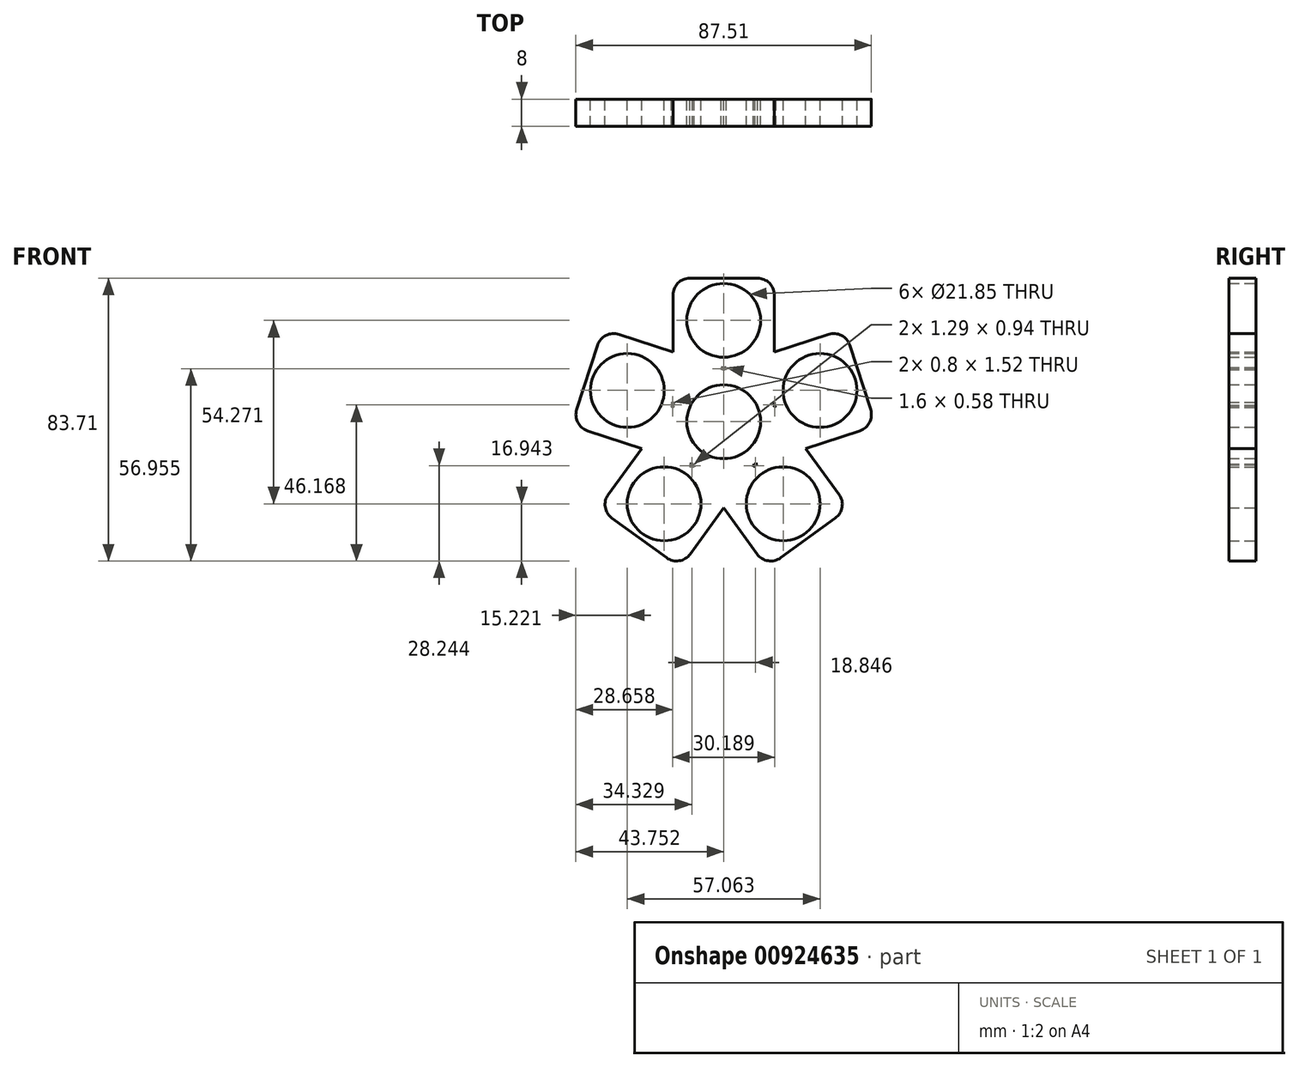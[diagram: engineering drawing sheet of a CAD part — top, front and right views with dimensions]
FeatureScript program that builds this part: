
annotation { "Feature Type Name" : "Feature", "Feature Type Description" : "" }
export const myFeature = defineFeature(function(context is Context, id is Id, definition is map)
    precondition{}
    {
        {
            var Q0;
            Q0=qCreatedBy(makeId("Front.planeOp"),FACE);
            var sketch = newSketch(context, id + "F0", { "sketchPlane" : qUnion([Q0])});
            skCircle(sketch, "E0", {"center": v(147.66, 55.6) * mm, "radius": 10.93 * mm});
            skLineSegment(sketch, "E1", {"start": v(147.66, 85.6) * mm, "end": v(147.66, 55.6) * mm, "construction": true});
            skCircle(sketch, "E2", {"center": v(147.66, 85.6) * mm, "radius": 10.93 * mm});
            skPoint(sketch, "E3", {"position": v(147.66, 70.6) * mm});
            skLineSegment(sketch, "E4.bottom", {"start": v(162.66, 43.1) * mm, "end": v(132.66, 43.1) * mm});
            skLineSegment(sketch, "E4.top", {"start": v(157.66, 98.1) * mm, "end": v(137.66, 98.1) * mm});
            skLineSegment(sketch, "E4.left", {"start": v(162.66, 43.1) * mm, "end": v(162.66, 93.1) * mm});
            skLineSegment(sketch, "E4.right", {"start": v(132.66, 43.1) * mm, "end": v(132.66, 93.1) * mm});
            skPoint(sketch, "E5.visualSharp", {"position": v(132.66, 98.1) * mm});
            skArc(sketch, "E5.filletArc", {"start": v(137.66, 98.1) * mm, "mid": v(134.13, 96.63) * mm, "end": v(132.66, 93.1) * mm});
            skPoint(sketch, "E6.visualSharp", {"position": v(162.66, 98.1) * mm});
            skArc(sketch, "E6.filletArc", {"start": v(162.66, 93.1) * mm, "mid": v(161.2, 96.63) * mm, "end": v(157.66, 98.1) * mm});
            skPoint(sketch, "E7.1.0", {"position": v(102.6, 54.46) * mm});
            skLineSegment(sketch, "E7.1.1", {"start": v(119.13, 64.86) * mm, "end": v(147.66, 55.6) * mm, "construction": true});
            skLineSegment(sketch, "E7.1.2", {"start": v(110.33, 78.24) * mm, "end": v(104.15, 59.22) * mm});
            skLineSegment(sketch, "E7.1.3", {"start": v(154.92, 37.47) * mm, "end": v(107.36, 52.92) * mm});
            skPoint(sketch, "E7.1.4", {"position": v(111.88, 83) * mm});
            skArc(sketch, "E7.1.5", {"start": v(116.63, 81.45) * mm, "mid": v(112.82, 81.15) * mm, "end": v(110.33, 78.24) * mm});
            skLineSegment(sketch, "E7.1.7", {"start": v(164.19, 66) * mm, "end": v(116.63, 81.45) * mm});
            skLineSegment(sketch, "E7.1.8", {"start": v(164.19, 66) * mm, "end": v(154.92, 37.47) * mm});
            skCircle(sketch, "E7.1.9", {"center": v(119.13, 64.86) * mm, "radius": 10.92 * mm});
            skPoint(sketch, "E7.1.10", {"position": v(133.4, 60.23) * mm});
            skPoint(sketch, "E7.1.11", {"position": v(133.4, 60.23) * mm});
            skArc(sketch, "E7.1.12", {"start": v(104.15, 59.22) * mm, "mid": v(104.45, 55.4) * mm, "end": v(107.36, 52.92) * mm});
            skPoint(sketch, "E7.2.0", {"position": v(134.82, 12.4) * mm});
            skLineSegment(sketch, "E7.2.1", {"start": v(130.03, 31.32) * mm, "end": v(147.66, 55.6) * mm, "construction": true});
            skLineSegment(sketch, "E7.2.2", {"start": v(114.6, 27.09) * mm, "end": v(130.77, 15.33) * mm});
            skLineSegment(sketch, "E7.2.3", {"start": v(167.15, 56.89) * mm, "end": v(137.76, 16.44) * mm});
            skPoint(sketch, "E7.2.4", {"position": v(110.55, 30.03) * mm});
            skArc(sketch, "E7.2.5", {"start": v(113.49, 34.07) * mm, "mid": v(112.6, 30.35) * mm, "end": v(114.6, 27.09) * mm});
            skLineSegment(sketch, "E7.2.7", {"start": v(142.87, 74.52) * mm, "end": v(113.49, 34.07) * mm});
            skLineSegment(sketch, "E7.2.8", {"start": v(142.87, 74.52) * mm, "end": v(167.15, 56.89) * mm});
            skCircle(sketch, "E7.2.9", {"center": v(130.03, 31.32) * mm, "radius": 10.93 * mm});
            skPoint(sketch, "E7.2.10", {"position": v(138.85, 43.46) * mm});
            skPoint(sketch, "E7.2.11", {"position": v(138.85, 43.46) * mm});
            skArc(sketch, "E7.2.12", {"start": v(130.77, 15.33) * mm, "mid": v(134.5, 14.44) * mm, "end": v(137.76, 16.44) * mm});
            skLineSegment(sketch, "E8.1.3.0", {"start": v(165.3, 31.32) * mm, "end": v(147.66, 55.6) * mm, "construction": true});
            skLineSegment(sketch, "E8.4.3.0", {"start": v(164.55, 15.33) * mm, "end": v(180.73, 27.09) * mm});
            skLineSegment(sketch, "E8.7.3.0", {"start": v(152.45, 74.52) * mm, "end": v(181.84, 34.07) * mm});
            skPoint(sketch, "E8.8.3.0", {"position": v(184.78, 30.03) * mm});
            skPoint(sketch, "E8.10.3.0", {"position": v(160.5, 12.4) * mm});
            skArc(sketch, "E8.11.3.0", {"start": v(157.57, 16.44) * mm, "mid": v(160.83, 14.44) * mm, "end": v(164.55, 15.33) * mm});
            skLineSegment(sketch, "E8.17.3.0", {"start": v(128.18, 56.89) * mm, "end": v(157.57, 16.44) * mm});
            skLineSegment(sketch, "E8.20.3.0", {"start": v(128.18, 56.89) * mm, "end": v(152.45, 74.52) * mm});
            skCircle(sketch, "E8.23.3.0", {"center": v(165.3, 31.32) * mm, "radius": 10.93 * mm});
            skPoint(sketch, "E8.25.3.0", {"position": v(156.48, 43.46) * mm});
            skPoint(sketch, "E8.26.3.0", {"position": v(156.48, 43.46) * mm});
            skArc(sketch, "E8.27.3.0", {"start": v(180.73, 27.09) * mm, "mid": v(182.73, 30.35) * mm, "end": v(181.84, 34.07) * mm});
            skLineSegment(sketch, "E8.1.4.0", {"start": v(176.2, 64.86) * mm, "end": v(147.66, 55.6) * mm, "construction": true});
            skLineSegment(sketch, "E8.4.4.0", {"start": v(191.17, 59.22) * mm, "end": v(185, 78.24) * mm});
            skLineSegment(sketch, "E8.7.4.0", {"start": v(131.14, 66) * mm, "end": v(178.7, 81.45) * mm});
            skPoint(sketch, "E8.8.4.0", {"position": v(183.45, 83) * mm});
            skPoint(sketch, "E8.10.4.0", {"position": v(192.72, 54.46) * mm});
            skArc(sketch, "E8.11.4.0", {"start": v(187.96, 52.92) * mm, "mid": v(190.87, 55.4) * mm, "end": v(191.17, 59.22) * mm});
            skLineSegment(sketch, "E8.17.4.0", {"start": v(140.4, 37.47) * mm, "end": v(187.96, 52.92) * mm});
            skLineSegment(sketch, "E8.20.4.0", {"start": v(140.4, 37.47) * mm, "end": v(131.14, 66) * mm});
            skCircle(sketch, "E8.23.4.0", {"center": v(176.2, 64.86) * mm, "radius": 10.93 * mm});
            skPoint(sketch, "E8.25.4.0", {"position": v(161.93, 60.23) * mm});
            skPoint(sketch, "E8.26.4.0", {"position": v(161.93, 60.23) * mm});
            skArc(sketch, "E8.27.4.0", {"start": v(185, 78.24) * mm, "mid": v(182.5, 81.15) * mm, "end": v(178.7, 81.45) * mm});
            skSolve(sketch);
        }
        {
            var Q0;
            {var subQ0=sQuery(id+"F0.wireOp",EDGE,"E8.17.3.0");var subQ1=sQuery(id+"F0.wireOp",EDGE,"E4.bottom");var subQ2=makeQuery(id+"F0.imprint","INTERSECT",VERTEX,{"derivedFrom":[subQ1,subQ0]});Q0=makeQuery(id+"F0.imprint","IMPRINT",FACE,{"disambiguationData":[TD([[makeQuery(id+"F0.imprint","IMPRINT",EDGE,{"disambiguationData":[TD([[subQ2,-1.0]])],"derivedFrom":subQ1}),-1.0]])]});}
            var Q1;
            {var subQ0=sQuery(id+"F0.wireOp",EDGE,"E7.1.7");var subQ1=sQuery(id+"F0.wireOp",EDGE,"E4.right");var subQ2=makeQuery(id+"F0.imprint","INTERSECT",VERTEX,{"derivedFrom":[subQ1,subQ0]});Q1=makeQuery(id+"F0.imprint","IMPRINT",FACE,{"disambiguationData":[TD([[makeQuery(id+"F0.imprint","IMPRINT",EDGE,{"disambiguationData":[TD([[subQ2,1.0]])],"derivedFrom":subQ1}),-1.0]])]});}
            var Q2;
            Q2=makeQuery(id+"F0.imprint","IMPRINT",FACE,{"disambiguationData":[TD([[makeQuery(id+"F0.imprint","IMPRINT",EDGE,{"derivedFrom":sQuery(id+"F0.wireOp",EDGE,"E2")}),-1.0]])]});
            var Q3;
            {var subQ0=sQuery(id+"F0.wireOp",EDGE,"E8.7.4.0");var subQ1=sQuery(id+"F0.wireOp",EDGE,"E4.left");var subQ2=makeQuery(id+"F0.imprint","INTERSECT",VERTEX,{"derivedFrom":[subQ1,subQ0]});Q3=makeQuery(id+"F0.imprint","IMPRINT",FACE,{"disambiguationData":[TD([[makeQuery(id+"F0.imprint","IMPRINT",EDGE,{"disambiguationData":[TD([[subQ2,1.0]])],"derivedFrom":subQ1}),1.0]])]});}
            var Q4;
            {var subQ0=sQuery(id+"F0.wireOp",EDGE,"E8.7.3.0");var subQ1=sQuery(id+"F0.wireOp",EDGE,"E7.1.7");var subQ2=makeQuery(id+"F0.imprint","INTERSECT",VERTEX,{"derivedFrom":[subQ1,subQ0]});Q4=makeQuery(id+"F0.imprint","IMPRINT",FACE,{"disambiguationData":[TD([[makeQuery(id+"F0.imprint","IMPRINT",EDGE,{"disambiguationData":[TD([[subQ2,-1.0]])],"derivedFrom":subQ1}),-1.0]])]});}
            var Q5;
            Q5=makeQuery(id+"F0.imprint","IMPRINT",FACE,{"disambiguationData":[TD([[makeQuery(id+"F0.imprint","IMPRINT",EDGE,{"derivedFrom":sQuery(id+"F0.wireOp",EDGE,"E0")}),-1.0]])]});
            var Q6;
            {var subQ0=sQuery(id+"F0.wireOp",EDGE,"E7.2.3");var subQ1=sQuery(id+"F0.wireOp",EDGE,"E7.1.3");var subQ2=makeQuery(id+"F0.imprint","INTERSECT",VERTEX,{"derivedFrom":[subQ1,subQ0]});Q6=makeQuery(id+"F0.imprint","IMPRINT",FACE,{"disambiguationData":[TD([[makeQuery(id+"F0.imprint","IMPRINT",EDGE,{"disambiguationData":[TD([[subQ2,-1.0]])],"derivedFrom":subQ1}),1.0]])]});}
            var Q7;
            Q7=makeQuery(id+"F0.imprint","IMPRINT",FACE,{"disambiguationData":[TD([[makeQuery(id+"F0.imprint","IMPRINT",EDGE,{"derivedFrom":sQuery(id+"F0.wireOp",EDGE,"E7.2.2")}),1.0]])]});
            var Q8;
            Q8=makeQuery(id+"F0.imprint","IMPRINT",FACE,{"disambiguationData":[TD([[makeQuery(id+"F0.imprint","IMPRINT",EDGE,{"derivedFrom":sQuery(id+"F0.wireOp",EDGE,"E8.4.3.0")}),1.0]])]});
            var Q9;
            Q9=makeQuery(id+"F0.imprint","IMPRINT",FACE,{"disambiguationData":[TD([[makeQuery(id+"F0.imprint","IMPRINT",EDGE,{"derivedFrom":sQuery(id+"F0.wireOp",EDGE,"E8.4.4.0")}),1.0]])]});
            var Q10;
            {var subQ0=sQuery(id+"F0.wireOp",EDGE,"E8.17.4.0");var subQ1=sQuery(id+"F0.wireOp",EDGE,"E4.left");var subQ2=makeQuery(id+"F0.imprint","INTERSECT",VERTEX,{"derivedFrom":[subQ1,subQ0]});Q10=makeQuery(id+"F0.imprint","IMPRINT",FACE,{"disambiguationData":[TD([[makeQuery(id+"F0.imprint","IMPRINT",EDGE,{"disambiguationData":[TD([[subQ2,-1.0]])],"derivedFrom":subQ1}),-1.0]])]});}
            var Q11;
            {var subQ0=sQuery(id+"F0.wireOp",EDGE,"E7.2.3");var subQ1=sQuery(id+"F0.wireOp",EDGE,"E4.left");var subQ2=makeQuery(id+"F0.imprint","INTERSECT",VERTEX,{"derivedFrom":[subQ1,subQ0]});Q11=makeQuery(id+"F0.imprint","IMPRINT",FACE,{"disambiguationData":[TD([[makeQuery(id+"F0.imprint","IMPRINT",EDGE,{"disambiguationData":[TD([[subQ2,-1.0]])],"derivedFrom":subQ1}),-1.0]])]});}
            var Q12;
            {var subQ0=sQuery(id+"F0.wireOp",EDGE,"E7.2.8");var subQ1=sQuery(id+"F0.wireOp",EDGE,"E7.2.3");var subQ2=makeQuery(id+"F0.imprint","INTERSECT",VERTEX,{"derivedFrom":[subQ1,subQ0]});Q12=makeQuery(id+"F0.imprint","IMPRINT",FACE,{"disambiguationData":[TD([[makeQuery(id+"F0.imprint","IMPRINT",EDGE,{"disambiguationData":[TD([[subQ2,-1.0]])],"derivedFrom":subQ1}),-1.0]])]});}
            var Q13;
            {var subQ0=sQuery(id+"F0.wireOp",EDGE,"E7.2.3");var subQ1=sQuery(id+"F0.wireOp",EDGE,"E4.bottom");var subQ2=makeQuery(id+"F0.imprint","INTERSECT",VERTEX,{"derivedFrom":[subQ1,subQ0]});Q13=makeQuery(id+"F0.imprint","IMPRINT",FACE,{"disambiguationData":[TD([[makeQuery(id+"F0.imprint","IMPRINT",EDGE,{"disambiguationData":[TD([[subQ2,-1.0]])],"derivedFrom":subQ1}),-1.0]])]});}
            var Q14;
            {var subQ0=sQuery(id+"F0.wireOp",EDGE,"E8.17.4.0");var subQ1=sQuery(id+"F0.wireOp",EDGE,"E4.bottom");var subQ2=makeQuery(id+"F0.imprint","INTERSECT",VERTEX,{"derivedFrom":[subQ1,subQ0]});Q14=makeQuery(id+"F0.imprint","IMPRINT",FACE,{"disambiguationData":[TD([[makeQuery(id+"F0.imprint","IMPRINT",EDGE,{"disambiguationData":[TD([[subQ2,-1.0]])],"derivedFrom":subQ1}),-1.0]])]});}
            var Q15;
            {var subQ0=sQuery(id+"F0.wireOp",EDGE,"E4.left");var subQ1=sQuery(id+"F0.wireOp",EDGE,"E4.bottom");var subQ2=makeQuery(id+"F0.imprint","INTERSECT",VERTEX,{"derivedFrom":[subQ1,subQ0]});Q15=makeQuery(id+"F0.imprint","IMPRINT",FACE,{"disambiguationData":[TD([[makeQuery(id+"F0.imprint","IMPRINT",EDGE,{"disambiguationData":[TD([[subQ2,-1.0]])],"derivedFrom":subQ1}),-1.0]])]});}
            var Q16;
            {var subQ0=sQuery(id+"F0.wireOp",EDGE,"E7.1.8");var subQ1=sQuery(id+"F0.wireOp",EDGE,"E7.1.3");var subQ2=makeQuery(id+"F0.imprint","INTERSECT",VERTEX,{"derivedFrom":[subQ1,subQ0]});Q16=makeQuery(id+"F0.imprint","IMPRINT",FACE,{"disambiguationData":[TD([[makeQuery(id+"F0.imprint","IMPRINT",EDGE,{"disambiguationData":[TD([[subQ2,-1.0]])],"derivedFrom":subQ1}),-1.0]])]});}
            var Q17;
            {var subQ0=sQuery(id+"F0.wireOp",EDGE,"E7.2.3");var subQ1=sQuery(id+"F0.wireOp",EDGE,"E7.1.3");var subQ2=makeQuery(id+"F0.imprint","INTERSECT",VERTEX,{"derivedFrom":[subQ1,subQ0]});Q17=makeQuery(id+"F0.imprint","IMPRINT",FACE,{"disambiguationData":[TD([[makeQuery(id+"F0.imprint","IMPRINT",EDGE,{"disambiguationData":[TD([[subQ2,-1.0]])],"derivedFrom":subQ1}),-1.0]])]});}
            var Q18;
            {var subQ3=sQuery(id+"F0.wireOp",EDGE,"E7.1.8");var subQ7=sQuery(id+"F0.wireOp",EDGE,"E4.bottom");var subQ9=makeQuery(id+"F0.imprint","INTERSECT",VERTEX,{"derivedFrom":[subQ7,subQ3]});Q18=makeQuery(id+"F0.imprint","IMPRINT",FACE,{"disambiguationData":[TD([[makeQuery(id+"F0.imprint","IMPRINT",EDGE,{"disambiguationData":[TD([[subQ9,-1.0]])],"derivedFrom":subQ7}),1.0]])]});}
            var Q19;
            {var subQ0=sQuery(id+"F0.wireOp",EDGE,"E8.17.4.0");var subQ1=sQuery(id+"F0.wireOp",EDGE,"E7.1.3");var subQ2=makeQuery(id+"F0.imprint","INTERSECT",VERTEX,{"derivedFrom":[subQ1,subQ0]});Q19=makeQuery(id+"F0.imprint","IMPRINT",FACE,{"disambiguationData":[TD([[makeQuery(id+"F0.imprint","IMPRINT",EDGE,{"disambiguationData":[TD([[subQ2,-1.0]])],"derivedFrom":subQ1}),1.0]])]});}
            var Q20;
            {var subQ0=sQuery(id+"F0.wireOp",EDGE,"E8.20.4.0");var subQ1=sQuery(id+"F0.wireOp",EDGE,"E8.17.3.0");var subQ2=makeQuery(id+"F0.imprint","INTERSECT",VERTEX,{"derivedFrom":[subQ1,subQ0]});Q20=makeQuery(id+"F0.imprint","IMPRINT",FACE,{"disambiguationData":[TD([[makeQuery(id+"F0.imprint","IMPRINT",EDGE,{"disambiguationData":[TD([[subQ2,-1.0]])],"derivedFrom":subQ1}),-1.0]])]});}
            var Q21;
            {var subQ3=sQuery(id+"F0.wireOp",EDGE,"E8.20.4.0");var subQ6=sQuery(id+"F0.wireOp",EDGE,"E4.bottom");var subQ9=makeQuery(id+"F0.imprint","INTERSECT",VERTEX,{"derivedFrom":[subQ6,subQ3]});Q21=makeQuery(id+"F0.imprint","IMPRINT",FACE,{"disambiguationData":[TD([[makeQuery(id+"F0.imprint","IMPRINT",EDGE,{"disambiguationData":[TD([[subQ9,-1.0]])],"derivedFrom":subQ6}),-1.0]])]});}
            var Q22;
            {var subQ0=sQuery(id+"F0.wireOp",EDGE,"E4.right");var subQ1=sQuery(id+"F0.wireOp",EDGE,"E4.bottom");var subQ2=makeQuery(id+"F0.imprint","INTERSECT",VERTEX,{"derivedFrom":[subQ1,subQ0]});Q22=makeQuery(id+"F0.imprint","IMPRINT",FACE,{"disambiguationData":[TD([[makeQuery(id+"F0.imprint","IMPRINT",EDGE,{"disambiguationData":[TD([[subQ2,1.0]])],"derivedFrom":subQ1}),-1.0]])]});}
            var Q23;
            {var subQ0=sQuery(id+"F0.wireOp",EDGE,"E7.1.3");var subQ1=sQuery(id+"F0.wireOp",EDGE,"E4.right");var subQ2=makeQuery(id+"F0.imprint","INTERSECT",VERTEX,{"derivedFrom":[subQ1,subQ0]});Q23=makeQuery(id+"F0.imprint","IMPRINT",FACE,{"disambiguationData":[TD([[makeQuery(id+"F0.imprint","IMPRINT",EDGE,{"disambiguationData":[TD([[subQ2,-1.0]])],"derivedFrom":subQ1}),1.0]])]});}
            var Q24;
            {var subQ0=sQuery(id+"F0.wireOp",EDGE,"E8.17.3.0");var subQ1=sQuery(id+"F0.wireOp",EDGE,"E4.right");var subQ2=makeQuery(id+"F0.imprint","INTERSECT",VERTEX,{"derivedFrom":[subQ1,subQ0]});Q24=makeQuery(id+"F0.imprint","IMPRINT",FACE,{"disambiguationData":[TD([[makeQuery(id+"F0.imprint","IMPRINT",EDGE,{"disambiguationData":[TD([[subQ2,-1.0]])],"derivedFrom":subQ1}),1.0]])]});}
            var Q25;
            {var subQ0=sQuery(id+"F0.wireOp",EDGE,"E8.20.3.0");var subQ1=sQuery(id+"F0.wireOp",EDGE,"E7.2.7");var subQ2=makeQuery(id+"F0.imprint","INTERSECT",VERTEX,{"derivedFrom":[subQ1,subQ0]});Q25=makeQuery(id+"F0.imprint","IMPRINT",FACE,{"disambiguationData":[TD([[makeQuery(id+"F0.imprint","IMPRINT",EDGE,{"disambiguationData":[TD([[subQ2,-1.0]])],"derivedFrom":subQ1}),-1.0]])]});}
            var Q26;
            {var subQ0=sQuery(id+"F0.wireOp",EDGE,"E8.20.4.0");var subQ1=sQuery(id+"F0.wireOp",EDGE,"E4.right");var subQ2=makeQuery(id+"F0.imprint","INTERSECT",VERTEX,{"derivedFrom":[subQ1,subQ0]});Q26=makeQuery(id+"F0.imprint","IMPRINT",FACE,{"disambiguationData":[TD([[makeQuery(id+"F0.imprint","IMPRINT",EDGE,{"disambiguationData":[TD([[subQ2,-1.0]])],"derivedFrom":subQ1}),-1.0]])]});}
            var Q27;
            {var subQ0=sQuery(id+"F0.wireOp",EDGE,"E8.20.4.0");var subQ1=sQuery(id+"F0.wireOp",EDGE,"E4.right");var subQ2=makeQuery(id+"F0.imprint","INTERSECT",VERTEX,{"derivedFrom":[subQ1,subQ0]});Q27=makeQuery(id+"F0.imprint","IMPRINT",FACE,{"disambiguationData":[TD([[makeQuery(id+"F0.imprint","IMPRINT",EDGE,{"disambiguationData":[TD([[subQ2,-1.0]])],"derivedFrom":subQ1}),1.0]])]});}
            var Q28;
            {var subQ5=sQuery(id+"F0.wireOp",EDGE,"E8.7.4.0");var subQ7=sQuery(id+"F0.wireOp",EDGE,"E7.2.7");var subQ8=makeQuery(id+"F0.imprint","INTERSECT",VERTEX,{"derivedFrom":[subQ7,subQ5]});Q28=makeQuery(id+"F0.imprint","IMPRINT",FACE,{"disambiguationData":[TD([[makeQuery(id+"F0.imprint","IMPRINT",EDGE,{"disambiguationData":[TD([[subQ8,-1.0]])],"derivedFrom":subQ7}),1.0]])]});}
            var Q29;
            {var subQ0=sQuery(id+"F0.wireOp",EDGE,"E7.2.8");var subQ1=sQuery(id+"F0.wireOp",EDGE,"E7.1.7");var subQ2=makeQuery(id+"F0.imprint","INTERSECT",VERTEX,{"derivedFrom":[subQ1,subQ0]});Q29=makeQuery(id+"F0.imprint","IMPRINT",FACE,{"disambiguationData":[TD([[makeQuery(id+"F0.imprint","IMPRINT",EDGE,{"disambiguationData":[TD([[subQ2,-1.0]])],"derivedFrom":subQ1}),-1.0]])]});}
            var Q30;
            {var subQ0=sQuery(id+"F0.wireOp",EDGE,"E7.2.8");var subQ1=sQuery(id+"F0.wireOp",EDGE,"E7.1.7");var subQ2=makeQuery(id+"F0.imprint","INTERSECT",VERTEX,{"derivedFrom":[subQ1,subQ0]});Q30=makeQuery(id+"F0.imprint","IMPRINT",FACE,{"disambiguationData":[TD([[makeQuery(id+"F0.imprint","IMPRINT",EDGE,{"disambiguationData":[TD([[subQ2,-1.0]])],"derivedFrom":subQ1}),1.0]])]});}
            var Q31;
            {var subQ5=sQuery(id+"F0.wireOp",EDGE,"E8.7.3.0");var subQ7=sQuery(id+"F0.wireOp",EDGE,"E7.1.7");var subQ8=makeQuery(id+"F0.imprint","INTERSECT",VERTEX,{"derivedFrom":[subQ7,subQ5]});Q31=makeQuery(id+"F0.imprint","IMPRINT",FACE,{"disambiguationData":[TD([[makeQuery(id+"F0.imprint","IMPRINT",EDGE,{"disambiguationData":[TD([[subQ8,-1.0]])],"derivedFrom":subQ7}),1.0]])]});}
            var Q32;
            {var subQ0=sQuery(id+"F0.wireOp",EDGE,"E7.1.8");var subQ1=sQuery(id+"F0.wireOp",EDGE,"E4.left");var subQ2=makeQuery(id+"F0.imprint","INTERSECT",VERTEX,{"derivedFrom":[subQ1,subQ0]});Q32=makeQuery(id+"F0.imprint","IMPRINT",FACE,{"disambiguationData":[TD([[makeQuery(id+"F0.imprint","IMPRINT",EDGE,{"disambiguationData":[TD([[subQ2,-1.0]])],"derivedFrom":subQ1}),1.0]])]});}
            var Q33;
            {var subQ0=sQuery(id+"F0.wireOp",EDGE,"E7.1.8");var subQ1=sQuery(id+"F0.wireOp",EDGE,"E4.left");var subQ2=makeQuery(id+"F0.imprint","INTERSECT",VERTEX,{"derivedFrom":[subQ1,subQ0]});Q33=makeQuery(id+"F0.imprint","IMPRINT",FACE,{"disambiguationData":[TD([[makeQuery(id+"F0.imprint","IMPRINT",EDGE,{"disambiguationData":[TD([[subQ2,-1.0]])],"derivedFrom":subQ1}),-1.0]])]});}
            var Q34;
            {var subQ0=sQuery(id+"F0.wireOp",EDGE,"E8.20.3.0");var subQ1=sQuery(id+"F0.wireOp",EDGE,"E8.7.3.0");var subQ2=makeQuery(id+"F0.imprint","INTERSECT",VERTEX,{"derivedFrom":[subQ1,subQ0]});Q34=makeQuery(id+"F0.imprint","IMPRINT",FACE,{"disambiguationData":[TD([[makeQuery(id+"F0.imprint","IMPRINT",EDGE,{"disambiguationData":[TD([[subQ2,-1.0]])],"derivedFrom":subQ1}),-1.0]])]});}
            var Q35;
            Q35=makeQuery(id+"F0.imprint","IMPRINT",FACE,{"disambiguationData":[TD([[makeQuery(id+"F0.imprint","IMPRINT",EDGE,{"derivedFrom":sQuery(id+"F0.wireOp",EDGE,"E7.1.2")}),1.0]])]});
            extrude(context, id + "F1", {"entities" : qUnion([Q0, Q1, Q2, Q3, Q4, Q5, Q6, Q7, Q8, Q9, Q10, Q11, Q12, Q13, Q14, Q15, Q16, Q17, Q18, Q19, Q20, Q21, Q22, Q23, Q24, Q25, Q26, Q27, Q28, Q29, Q30, Q31, Q32, Q33, Q34, Q35]), "depth" : 8 * mm, "offsetDistance" : 25 * mm});
        }
    });
